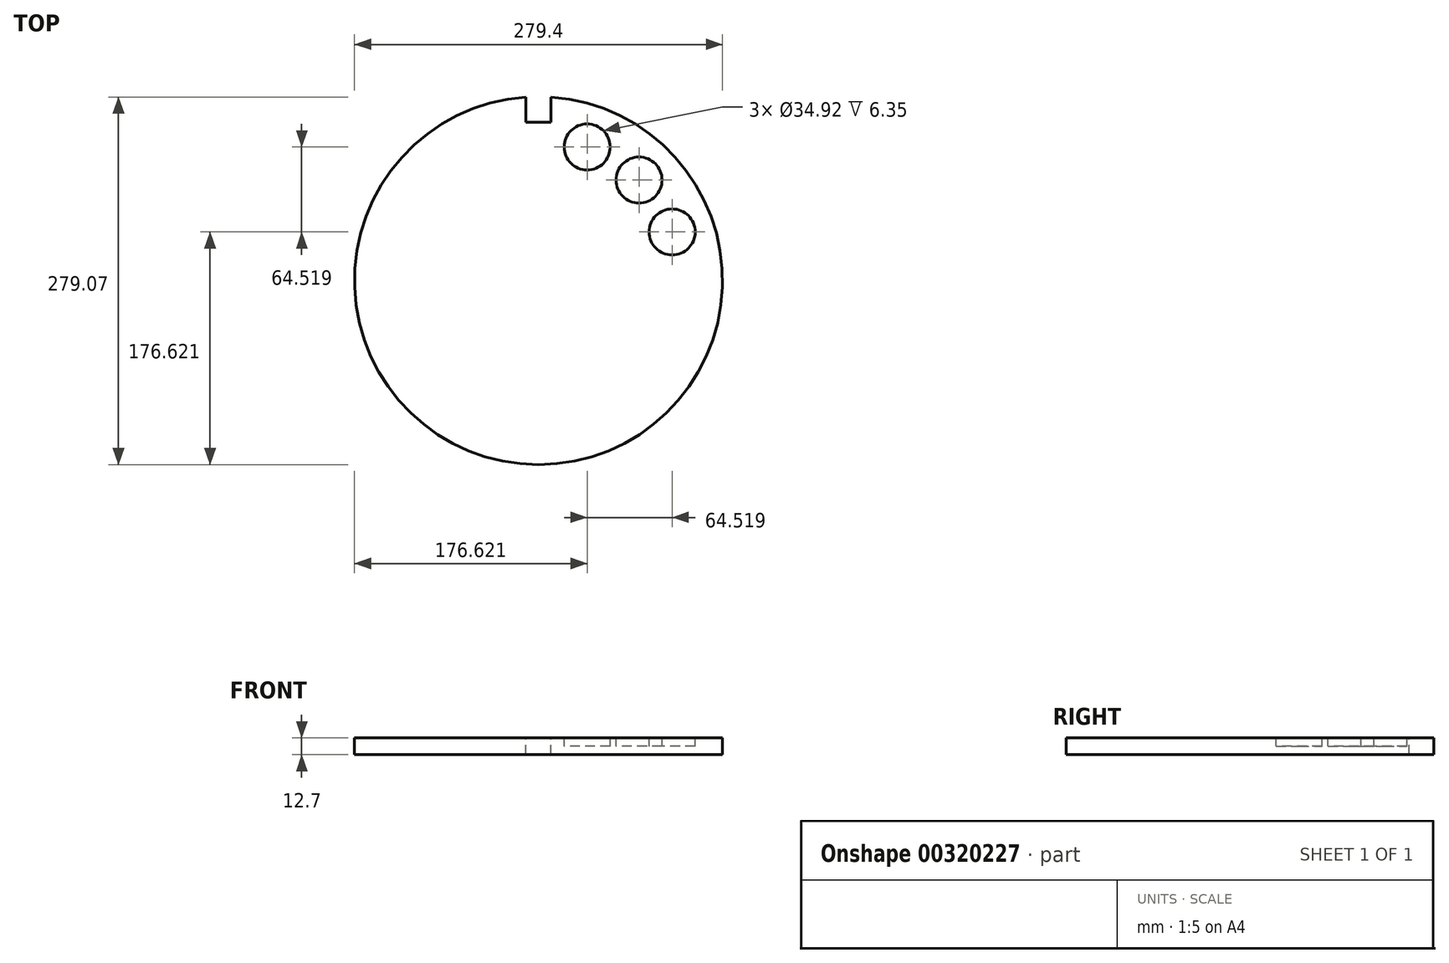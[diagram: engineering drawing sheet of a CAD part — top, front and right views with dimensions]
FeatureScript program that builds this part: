
annotation { "Feature Type Name" : "Feature", "Feature Type Description" : "" }
export const myFeature = defineFeature(function(context is Context, id is Id, definition is map)
    precondition{}
    {
        {
            var Q0;
            Q0=qCreatedBy(makeId("Top.planeOp"),FACE);
            var sketch = newSketch(context, id + "F0", { "sketchPlane" : qUnion([Q0])});
            skCircle(sketch, "E0", {"center": v(0, 0) * mm, "radius": 107.95 * mm, "construction": true});
            skCircle(sketch, "E1", {"center": v(0, 0) * mm, "radius": 139.7 * mm});
            skLineSegment(sketch, "E2", {"start": v(0, 0) * mm, "end": v(139.7, 0) * mm, "construction": true});
            skLineSegment(sketch, "E3", {"start": v(0, 0) * mm, "end": v(0, 139.7) * mm, "construction": true});
            skLineSegment(sketch, "E4", {"start": v(0, 0) * mm, "end": v(76.33, 76.33) * mm, "construction": true});
            skLineSegment(sketch, "E5", {"start": v(0, 0) * mm, "end": v(101.44, 36.92) * mm, "construction": true});
            skLineSegment(sketch, "E6", {"start": v(0, 0) * mm, "end": v(36.92, 101.44) * mm, "construction": true});
            skCircle(sketch, "E7", {"center": v(36.92, 101.44) * mm, "radius": 17.46 * mm});
            skCircle(sketch, "E8", {"center": v(76.33, 76.33) * mm, "radius": 17.46 * mm});
            skCircle(sketch, "E9", {"center": v(101.44, 36.92) * mm, "radius": 17.46 * mm});
            skLineSegment(sketch, "E10.top", {"start": v(-9.53, 113.97) * mm, "end": v(9.52, 113.97) * mm});
            skLineSegment(sketch, "E10.left", {"start": v(-9.53, 139.37) * mm, "end": v(-9.53, 113.97) * mm});
            skLineSegment(sketch, "E10.right", {"start": v(9.52, 139.37) * mm, "end": v(9.52, 113.97) * mm});
            skPoint(sketch, "E10.middle", {"position": v(0, 126.67) * mm});
            skLineSegment(sketch, "E11", {"start": v(-9.53, 120.32) * mm, "end": v(9.52, 120.32) * mm});
            skCircle(sketch, "E12", {"center": v(0, 0) * mm, "radius": 44.84 * mm});
            skSolve(sketch);
        }
        {
            var Q0;
            Q0 = qSketchRegion(id + "F0", true);
            var Q1;
            Q1=makeQuery(id+"F0.imprint","IMPRINT",FACE,{"disambiguationData":[TD([[makeQuery(id+"F0.imprint","IMPRINT",EDGE,{"derivedFrom":sQuery(id+"F0.wireOp",EDGE,"E7")}),1.0]])]});
            var Q2;
            Q2=makeQuery(id+"F0.imprint","IMPRINT",FACE,{"disambiguationData":[TD([[makeQuery(id+"F0.imprint","IMPRINT",EDGE,{"derivedFrom":sQuery(id+"F0.wireOp",EDGE,"E8")}),1.0]])]});
            var Q3;
            Q3=makeQuery(id+"F0.imprint","IMPRINT",FACE,{"disambiguationData":[TD([[makeQuery(id+"F0.imprint","IMPRINT",EDGE,{"derivedFrom":sQuery(id+"F0.wireOp",EDGE,"E9")}),1.0]])]});
            var Q4;
            {var subQ0=sQuery(id+"F0.wireOp",EDGE,"E10.top");Q4=makeQuery(id+"F0.imprint","IMPRINT",FACE,{"disambiguationData":[TD([[makeQuery(id+"F0.imprint","IMPRINT",EDGE,{"derivedFrom":subQ0}),1.0]])]});}
            var Q5;
            Q5=makeQuery(id+"F0.imprint","IMPRINT",FACE,{"disambiguationData":[TD([[makeQuery(id+"F0.imprint","IMPRINT",EDGE,{"derivedFrom":sQuery(id+"F0.wireOp",EDGE,"E12")}),1.0]])]});
            extrude(context, id + "F1", {"entities" : qUnion([Q0, Q1, Q2, Q3, Q4, Q5]), "oppositeDirection" : true, "depth" : 12.7 * mm});
        }
        {
            var Q0;
            Q0=makeQuery(id+"F0.imprint","IMPRINT",FACE,{"disambiguationData":[TD([[makeQuery(id+"F0.imprint","IMPRINT",EDGE,{"derivedFrom":sQuery(id+"F0.wireOp",EDGE,"E7")}),1.0]])]});
            var Q1;
            Q1=makeQuery(id+"F0.imprint","IMPRINT",FACE,{"disambiguationData":[TD([[makeQuery(id+"F0.imprint","IMPRINT",EDGE,{"derivedFrom":sQuery(id+"F0.wireOp",EDGE,"E8")}),1.0]])]});
            var Q2;
            Q2=makeQuery(id+"F0.imprint","IMPRINT",FACE,{"disambiguationData":[TD([[makeQuery(id+"F0.imprint","IMPRINT",EDGE,{"derivedFrom":sQuery(id+"F0.wireOp",EDGE,"E9")}),1.0]])]});
            extrude(context, id + "F2", {"entities" : qUnion([Q0, Q1, Q2]), "operationType" : NewBodyOperationType.REMOVE, "oppositeDirection" : true, "depth" : 6.35 * mm});
        }
        {
            var Q0;
            {var subQ5=sQuery(id+"F0.wireOp",EDGE,"E11");Q0=makeQuery(id+"F0.imprint","IMPRINT",FACE,{"disambiguationData":[TD([[makeQuery(id+"F0.imprint","IMPRINT",EDGE,{"derivedFrom":subQ5}),1.0]])]});}
            extrude(context, id + "F3", {"entities" : qUnion([Q0]), "operationType" : NewBodyOperationType.REMOVE, "endBound" : BoundingType.THROUGH_ALL, "oppositeDirection" : true, "depth" : 25.4 * mm});
        }
        {
            var Q0;
            Q0=qCreatedBy(makeId("Front.planeOp"),FACE);
            var sketch = newSketch(context, id + "F4", { "sketchPlane" : qUnion([Q0])});
            skLineSegment(sketch, "E13", {"start": v(0, 0) * mm, "end": v(0, 89.72) * mm, "construction": true});
            skSolve(sketch);
        }
    });
